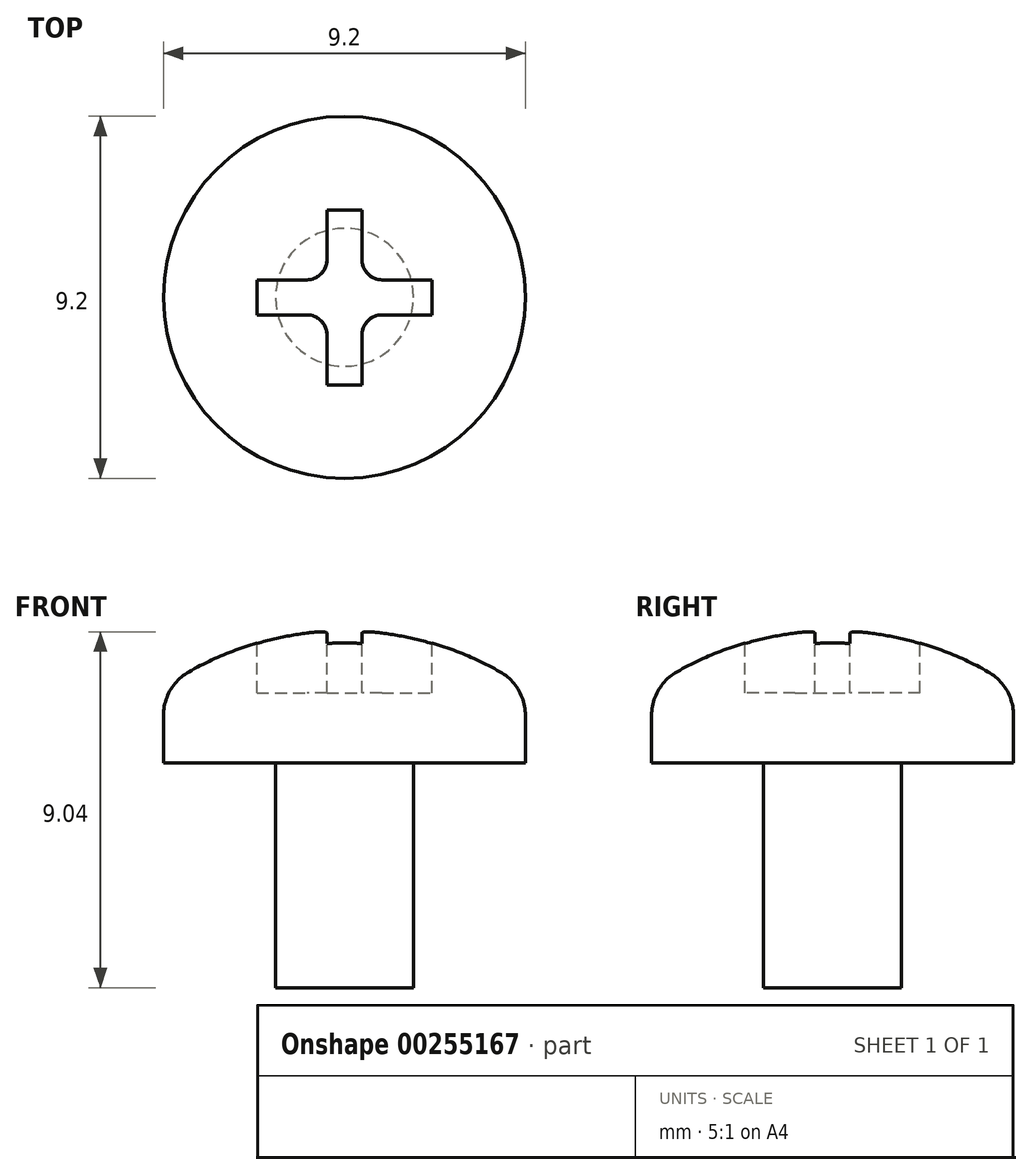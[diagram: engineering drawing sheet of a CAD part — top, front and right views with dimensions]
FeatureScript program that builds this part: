
annotation { "Feature Type Name" : "Feature", "Feature Type Description" : "" }
export const myFeature = defineFeature(function(context is Context, id is Id, definition is map)
    precondition{}
    {
        {
            var Q0;
            Q0=qCreatedBy(makeId("Top.planeOp"),FACE);
            var sketch = newSketch(context, id + "F0", { "sketchPlane" : qUnion([Q0])});
            skCircle(sketch, "E0", {"center": v(0, 0) * mm, "radius": 1.75 * mm});
            skSolve(sketch);
        }
        {
            var Q0;
            Q0 = qSketchRegion(id + "F0", true);
            extrude(context, id + "F1", {"entities" : qUnion([Q0]), "depth" : 5.7 * mm});
        }
        {
            var Q0;
            Q0=qCreatedBy(makeId("Right.planeOp"),FACE);
            var sketch = newSketch(context, id + "F2", { "sketchPlane" : qUnion([Q0])});
            skLineSegment(sketch, "E1", {"start": v(-4.6, 5.72) * mm, "end": v(0, 5.72) * mm});
            skLineSegment(sketch, "E2", {"start": v(0, 0) * mm, "end": v(0, 9.1) * mm, "construction": true});
            skLineSegment(sketch, "E3", {"start": v(0, 5.72) * mm, "end": v(0, 9.1) * mm});
            skLineSegment(sketch, "E4", {"start": v(-4.6, 5.72) * mm, "end": v(-4.6, 7.62) * mm});
            skArc(sketch, "E5", {"start": v(0, 9.1) * mm, "mid": v(-2.4, 8.7) * mm, "end": v(-4.6, 7.62) * mm});
            skSolve(sketch);
        }
        {
            var Q0;
            Q0 = qSketchRegion(id + "F2", true);
            var Q1;
            Q1=sQuery(id+"F2.wireOp",EDGE,"E2");
            revolve(context, id + "F3", {"operationType" : NewBodyOperationType.ADD, "entities" : qUnion([Q0]), "axis" : qUnion([Q1]), "revolveType" : RevolveType.FULL});
        }
        {
            var Q0;
            Q0=makeQuery(id+"F3.opRevolve","SWEPT_EDGE",EDGE,{"disambiguationData":[OSD([sQuery(id+"F2.wireOp",EDGE,"E4"),sQuery(id+"F2.wireOp",EDGE,"E5")])]});
            fillet(context, id + "F4", {"entities" : qUnion([Q0]), "radius" : 1.27 * mm, "tangentPropagation" : true, "allowEdgeOverflow" : false});
        }
        {
            var Q0;
            Q0=qCreatedBy(makeId("Top.planeOp"),FACE);
            cPlane(context, id + "F5", {"entities" : qUnion([Q0]), "cplaneType" : CPlaneType.OFFSET, "offset" : 10.4 * mm, "width" : 152.4 * mm, "height" : 152.4 * mm});
        }
        {
            var Q0;
            Q0=qCreatedBy(id+"F5.planeOp",FACE);
            var sketch = newSketch(context, id + "F6", { "sketchPlane" : qUnion([Q0])});
            skLineSegment(sketch, "E6.bottom", {"start": v(-2.22, -0.44) * mm, "end": v(-0.44, -0.44) * mm});
            skLineSegment(sketch, "E6.top", {"start": v(-2.22, 0.44) * mm, "end": v(-0.44, 0.44) * mm});
            skLineSegment(sketch, "E6.left", {"start": v(-2.22, -0.44) * mm, "end": v(-2.22, 0.44) * mm});
            skLineSegment(sketch, "E6.right", {"start": v(2.22, -0.44) * mm, "end": v(2.22, 0.44) * mm});
            skLineSegment(sketch, "E7.bottom", {"start": v(-0.44, 2.22) * mm, "end": v(0.44, 2.22) * mm});
            skLineSegment(sketch, "E7.top", {"start": v(-0.44, -2.22) * mm, "end": v(0.44, -2.22) * mm});
            skLineSegment(sketch, "E7.left", {"start": v(-0.44, 2.22) * mm, "end": v(-0.44, 0.44) * mm});
            skLineSegment(sketch, "E7.right", {"start": v(0.44, 2.22) * mm, "end": v(0.44, 0.44) * mm});
            skLineSegment(sketch, "E8.trimOffspring", {"start": v(-0.44, -0.44) * mm, "end": v(-0.44, -2.22) * mm});
            skLineSegment(sketch, "E9.trimOffspring", {"start": v(0.44, -0.44) * mm, "end": v(2.22, -0.44) * mm});
            skLineSegment(sketch, "E10.trimOffspring", {"start": v(0.44, -0.44) * mm, "end": v(0.44, -2.22) * mm});
            skLineSegment(sketch, "E11.trimOffspring", {"start": v(0.44, 0.44) * mm, "end": v(2.22, 0.44) * mm});
            skLineSegment(sketch, "E12", {"start": v(0, -2.22) * mm, "end": v(0, 2.22) * mm, "construction": true});
            skPoint(sketch, "E12.endSnap0", {"position": v(0, 2.22) * mm});
            skLineSegment(sketch, "E13", {"start": v(-2.22, 0) * mm, "end": v(2.22, 0) * mm, "construction": true});
            skSolve(sketch);
        }
        {
            var Q0;
            Q0 = qSketchRegion(id + "F6", true);
            extrude(context, id + "F7", {"entities" : qUnion([Q0]), "operationType" : NewBodyOperationType.REMOVE, "oppositeDirection" : true, "depth" : 2.92 * mm});
        }
        {
            var Q0;
            Q0=makeQuery(id+"F7.boolean.opBoolean","COPY",EDGE,{"derivedFrom":makeQuery(id+"F7.opExtrude","SWEPT_EDGE",EDGE,{"disambiguationData":[OSD([sQuery(id+"F6.wireOp",EDGE,"E6.top"),sQuery(id+"F6.wireOp",EDGE,"E7.left")])]})});
            var Q1;
            Q1=makeQuery(id+"F7.boolean.opBoolean","COPY",EDGE,{"derivedFrom":makeQuery(id+"F7.opExtrude","SWEPT_EDGE",EDGE,{"disambiguationData":[OSD([sQuery(id+"F6.wireOp",EDGE,"E7.right"),sQuery(id+"F6.wireOp",EDGE,"E11.trimOffspring")])]})});
            var Q2;
            Q2=makeQuery(id+"F7.boolean.opBoolean","COPY",EDGE,{"derivedFrom":makeQuery(id+"F7.opExtrude","SWEPT_EDGE",EDGE,{"disambiguationData":[OSD([sQuery(id+"F6.wireOp",EDGE,"E6.bottom"),sQuery(id+"F6.wireOp",EDGE,"E8.trimOffspring")])]})});
            var Q3;
            Q3=makeQuery(id+"F7.boolean.opBoolean","COPY",EDGE,{"derivedFrom":makeQuery(id+"F7.opExtrude","SWEPT_EDGE",EDGE,{"disambiguationData":[OSD([sQuery(id+"F6.wireOp",EDGE,"E9.trimOffspring"),sQuery(id+"F6.wireOp",EDGE,"E10.trimOffspring")])]})});
            fillet(context, id + "F8", {"entities" : qUnion([Q0, Q1, Q2, Q3]), "radius" : 0.5 * mm, "tangentPropagation" : true, "allowEdgeOverflow" : false});
        }
    });
